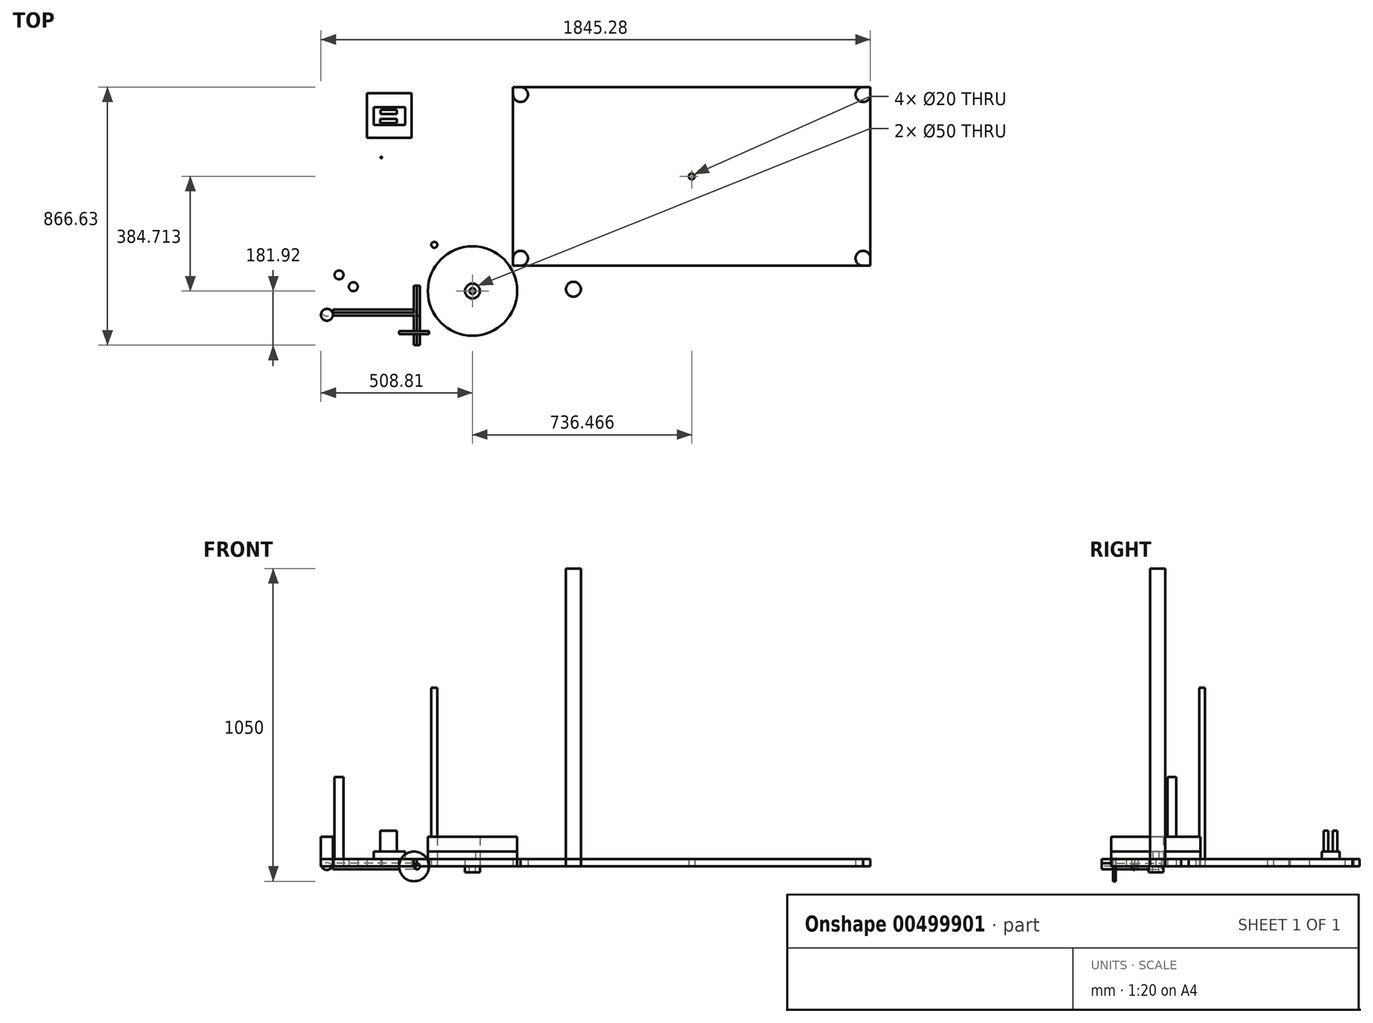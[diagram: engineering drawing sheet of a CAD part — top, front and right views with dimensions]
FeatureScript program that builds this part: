
annotation { "Feature Type Name" : "Feature", "Feature Type Description" : "" }
export const myFeature = defineFeature(function(context is Context, id is Id, definition is map)
    precondition{}
    {
        {
            var Q0;
            Q0=qCreatedBy(makeId("Top.planeOp"),FACE);
            var sketch = newSketch(context, id + "F0", { "sketchPlane" : qUnion([Q0])});
            skCircle(sketch, "E0", {"center": v(0, 0) * mm, "radius": 150 * mm});
            skCircle(sketch, "E1", {"center": v(0, 0) * mm, "radius": 25 * mm});
            skCircle(sketch, "E2", {"center": v(0, 0) * mm, "radius": 10 * mm});
            skCircle(sketch, "E3", {"center": v(-128.12, 155.18) * mm, "radius": 10 * mm});
            skLineSegment(sketch, "E4.bottom", {"start": v(1336.47, 684.71) * mm, "end": v(136.47, 684.71) * mm});
            skLineSegment(sketch, "E4.top", {"start": v(1336.47, 84.71) * mm, "end": v(136.47, 84.71) * mm});
            skLineSegment(sketch, "E4.left", {"start": v(1336.47, 684.71) * mm, "end": v(1336.47, 84.71) * mm});
            skLineSegment(sketch, "E4.right", {"start": v(136.47, 684.71) * mm, "end": v(136.47, 84.71) * mm});
            skCircle(sketch, "E5", {"center": v(161.47, 659.71) * mm, "radius": 25 * mm});
            skCircle(sketch, "E6", {"center": v(161.47, 109.71) * mm, "radius": 25 * mm});
            skCircle(sketch, "E7", {"center": v(1311.47, 659.71) * mm, "radius": 25 * mm});
            skCircle(sketch, "E8", {"center": v(1311.47, 109.71) * mm, "radius": 25 * mm});
            skCircle(sketch, "E9", {"center": v(736.47, 384.71) * mm, "radius": 10 * mm});
            skCircle(sketch, "E10", {"center": v(338.94, 6.05) * mm, "radius": 25 * mm});
            skCircle(sketch, "E11", {"center": v(-448.12, 53.9) * mm, "radius": 15 * mm});
            skCircle(sketch, "E12", {"center": v(-400.17, 14.47) * mm, "radius": 15 * mm});
            skCircle(sketch, "E13", {"center": v(-488.81, -79.96) * mm, "radius": 20 * mm});
            skLineSegment(sketch, "E14", {"start": v(-470.5, -71.92) * mm, "end": v(-191.05, -71.92) * mm});
            skLineSegment(sketch, "E15", {"start": v(-191.3, -81.92) * mm, "end": v(-468.9, -81.92) * mm});
            skLineSegment(sketch, "E16.bottom", {"start": v(-186.3, 18.08) * mm, "end": v(-196.3, 18.08) * mm});
            skLineSegment(sketch, "E16.top", {"start": v(-186.3, -181.92) * mm, "end": v(-196.3, -181.92) * mm});
            skLineSegment(sketch, "E16.left", {"start": v(-186.3, 18.08) * mm, "end": v(-186.3, -181.92) * mm});
            skLineSegment(sketch, "E16.right", {"start": v(-196.3, 18.08) * mm, "end": v(-196.3, -181.92) * mm});
            skPoint(sketch, "E16.middle", {"position": v(-191.3, -81.92) * mm});
            skLineSegment(sketch, "E17.bottom", {"start": v(-146.3, -144.4) * mm, "end": v(-246.3, -144.4) * mm});
            skLineSegment(sketch, "E17.top", {"start": v(-146.3, -134.4) * mm, "end": v(-246.3, -134.4) * mm});
            skLineSegment(sketch, "E17.left", {"start": v(-146.3, -144.4) * mm, "end": v(-146.3, -134.4) * mm});
            skLineSegment(sketch, "E17.right", {"start": v(-246.3, -144.4) * mm, "end": v(-246.3, -134.4) * mm});
            skPoint(sketch, "E17.middle", {"position": v(-196.3, -139.4) * mm});
            skLineSegment(sketch, "E18.right", {"start": v(-236.3, 0) * mm, "end": v(-236.3, 10) * mm});
            skPoint(sketch, "E18.middle", {"position": v(-186.3, 5) * mm});
            skCircle(sketch, "E19", {"center": v(-191.3, -81.92) * mm, "radius": 5 * mm});
            skLineSegment(sketch, "E20", {"start": v(-191.3, -181.92) * mm, "end": v(-191.3, 18.08) * mm});
            skPoint(sketch, "E21", {"position": v(-196.3, -134.4) * mm});
            skPoint(sketch, "E22", {"position": v(-186.3, -134.4) * mm});
            skPoint(sketch, "E23", {"position": v(-196.3, 0) * mm});
            skPoint(sketch, "E24", {"position": v(-186.3, 10) * mm});
            skPoint(sketch, "E25", {"position": v(1086.47, 434.71) * mm});
            skPoint(sketch, "E26", {"position": v(1186.47, 434.71) * mm});
            skPoint(sketch, "E27", {"position": v(1086.47, 334.71) * mm});
            skPoint(sketch, "E28", {"position": v(1186.47, 334.71) * mm});
            skLineSegment(sketch, "E29.bottom", {"start": v(-354.19, 664.69) * mm, "end": v(-204.19, 664.69) * mm});
            skLineSegment(sketch, "E29.top", {"start": v(-354.19, 514.69) * mm, "end": v(-204.19, 514.69) * mm});
            skLineSegment(sketch, "E29.left", {"start": v(-354.19, 664.69) * mm, "end": v(-354.19, 514.69) * mm});
            skLineSegment(sketch, "E29.right", {"start": v(-204.19, 664.69) * mm, "end": v(-204.19, 514.69) * mm});
            skPoint(sketch, "E30", {"position": v(-329.19, 639.69) * mm});
            skPoint(sketch, "E31", {"position": v(-229.19, 639.69) * mm});
            skPoint(sketch, "E32", {"position": v(-329.19, 539.69) * mm});
            skPoint(sketch, "E33", {"position": v(-229.19, 539.69) * mm});
            skLineSegment(sketch, "E34.bottom", {"start": v(-331.08, 616.75) * mm, "end": v(-225.59, 616.75) * mm});
            skLineSegment(sketch, "E34.top", {"start": v(-331.08, 557) * mm, "end": v(-225.59, 557) * mm});
            skLineSegment(sketch, "E34.left", {"start": v(-331.08, 616.75) * mm, "end": v(-331.08, 557) * mm});
            skLineSegment(sketch, "E34.right", {"start": v(-225.59, 616.75) * mm, "end": v(-225.59, 557) * mm});
            skLineSegment(sketch, "E35.bottom", {"start": v(-309.55, 578.54) * mm, "end": v(-254.11, 578.54) * mm});
            skLineSegment(sketch, "E35.top", {"start": v(-309.55, 564) * mm, "end": v(-254.11, 564) * mm});
            skLineSegment(sketch, "E35.left", {"start": v(-309.55, 578.54) * mm, "end": v(-309.55, 564) * mm});
            skLineSegment(sketch, "E35.right", {"start": v(-254.11, 578.54) * mm, "end": v(-254.11, 564) * mm});
            skLineSegment(sketch, "E36.bottom", {"start": v(-309.01, 594.15) * mm, "end": v(-253.58, 594.15) * mm});
            skLineSegment(sketch, "E36.top", {"start": v(-309.01, 608.68) * mm, "end": v(-253.58, 608.68) * mm});
            skLineSegment(sketch, "E36.left", {"start": v(-309.01, 594.15) * mm, "end": v(-309.01, 608.68) * mm});
            skLineSegment(sketch, "E36.right", {"start": v(-253.58, 594.15) * mm, "end": v(-253.58, 608.68) * mm});
            skCircle(sketch, "E37", {"center": v(-306.51, 448.4) * mm, "radius": 2.5 * mm});
            skSolve(sketch);
        }
        {
            var Q0;
            Q0=makeQuery(id+"F0.imprint","IMPRINT",FACE,{"disambiguationData":[TD([[makeQuery(id+"F0.imprint","IMPRINT",EDGE,{"derivedFrom":sQuery(id+"F0.wireOp",EDGE,"E0")}),1.0]])]});
            var Q1;
            Q1=makeQuery(id+"F0.imprint","IMPRINT",FACE,{"disambiguationData":[TD([[makeQuery(id+"F0.imprint","IMPRINT",EDGE,{"derivedFrom":sQuery(id+"F0.wireOp",EDGE,"E1")}),1.0]])]});
            extrude(context, id + "F1", {"entities" : qUnion([Q0, Q1]), "depth" : 50 * mm});
        }
        {
            var Q0;
            Q0=makeQuery(id+"F0.imprint","IMPRINT",FACE,{"disambiguationData":[TD([[makeQuery(id+"F0.imprint","IMPRINT",EDGE,{"derivedFrom":sQuery(id+"F0.wireOp",EDGE,"E1")}),1.0]])]});
            extrude(context, id + "F2", {"entities" : qUnion([Q0]), "oppositeDirection" : true, "depth" : 20 * mm});
        }
        {
            var Q0;
            Q0=makeQuery(id+"F0.imprint","IMPRINT",FACE,{"disambiguationData":[TD([[makeQuery(id+"F0.imprint","IMPRINT",EDGE,{"derivedFrom":sQuery(id+"F0.wireOp",EDGE,"E3")}),1.0]])]});
            var Q1;
            Q1=sQuery(id+"F0.wireOp",EDGE,"E3");
            extrude(context, id + "F3", {"entities" : qUnion([Q0]), "surfaceEntities" : qUnion([Q1]), "depth" : 600 * mm});
        }
        {
            var Q0;
            Q0=makeQuery(id+"F0.imprint","IMPRINT",FACE,{"disambiguationData":[TD([[makeQuery(id+"F0.imprint","IMPRINT",EDGE,{"derivedFrom":sQuery(id+"F0.wireOp",EDGE,"E9")}),-1.0]])]});
            extrude(context, id + "F4", {"entities" : qUnion([Q0]), "depth" : 25 * mm});
        }
        {
            var Q0;
            Q0=makeQuery(id+"F0.imprint","IMPRINT",FACE,{"disambiguationData":[TD([[makeQuery(id+"F0.imprint","IMPRINT",EDGE,{"derivedFrom":sQuery(id+"F0.wireOp",EDGE,"E10")}),1.0]])]});
            extrude(context, id + "F5", {"entities" : qUnion([Q0]), "depth" : 1000 * mm});
        }
        {
            var Q0;
            Q0=makeQuery(id+"F0.imprint","IMPRINT",FACE,{"disambiguationData":[TD([[makeQuery(id+"F0.imprint","IMPRINT",EDGE,{"derivedFrom":sQuery(id+"F0.wireOp",EDGE,"E11")}),1.0]])]});
            var Q1;
            Q1=sQuery(id+"F0.wireOp",EDGE,"E11");
            extrude(context, id + "F6", {"entities" : qUnion([Q0]), "surfaceEntities" : qUnion([Q1]), "depth" : 300 * mm});
        }
        {
            var Q0;
            {var subQ0=sQuery(id+"F0.wireOp",EDGE,"E13");var subQ1=makeQuery(id+"F0.imprint","INTERSECT",VERTEX,{"derivedFrom":[subQ0,sQuery(id+"F0.wireOp",EDGE,"E14")]});Q0=makeQuery(id+"F0.imprint","IMPRINT",FACE,{"disambiguationData":[TD([[makeQuery(id+"F0.imprint","IMPRINT",EDGE,{"disambiguationData":[TD([[subQ1,-1.0]])],"derivedFrom":subQ0}),1.0]])]});}
            var Q1;
            Q1=makeQuery(id+"F0.imprint","IMPRINT",FACE,{"disambiguationData":[TD([[makeQuery(id+"F0.imprint","IMPRINT",EDGE,{"derivedFrom":sQuery(id+"F0.wireOp",EDGE,"E1")}),-1.0]])]});
            var Q2;
            Q2 = qConstructionFilter(qBodyType(qCreatedBy(id + "F0" ,EDGE), BodyType.WIRE), ConstructionObject.NO);
            extrude(context, id + "F7", {"entities" : qUnion([Q0, Q1]), "surfaceEntities" : qUnion([Q2]), "depth" : 100 * mm});
        }
        {
            var Q0;
            {var subQ1=sQuery(id+"F0.wireOp",EDGE,"E14");Q0=makeQuery(id+"F0.imprint","IMPRINT",FACE,{"disambiguationData":[TD([[makeQuery(id+"F0.imprint","IMPRINT",EDGE,{"derivedFrom":subQ1}),-1.0]])]});}
            var Q1;
            Q1=sQuery(id+"F0.wireOp",EDGE,"E14");
            revolve(context, id + "F8", {"entities" : qUnion([Q0]), "axis" : qUnion([Q1]), "revolveType" : RevolveType.FULL});
        }
        {
            var Q0;
            {var subQ0=sQuery(id+"F0.wireOp",EDGE,"E18.bottom");var subQ1=sQuery(id+"F0.wireOp",EDGE,"E16.left");var subQ2=makeQuery(id+"F0.imprint","INTERSECT",VERTEX,{"derivedFrom":[subQ1,subQ0]});Q0=makeQuery(id+"F0.imprint","IMPRINT",FACE,{"disambiguationData":[TD([[makeQuery(id+"F0.imprint","IMPRINT",EDGE,{"disambiguationData":[TD([[subQ2,-1.0]])],"derivedFrom":subQ1}),-1.0]])]});}
            var Q1;
            {var subQ0=sQuery(id+"F0.wireOp",EDGE,"E16.left");var subQ1=sQuery(id+"F0.wireOp",EDGE,"E16.bottom");var subQ2=makeQuery(id+"F0.imprint","INTERSECT",VERTEX,{"derivedFrom":[subQ1,subQ0]});Q1=makeQuery(id+"F0.imprint","IMPRINT",FACE,{"disambiguationData":[TD([[makeQuery(id+"F0.imprint","IMPRINT",EDGE,{"disambiguationData":[TD([[subQ2,-1.0]])],"derivedFrom":subQ1}),1.0]])]});}
            var Q2;
            {var subQ0=sQuery(id+"F0.wireOp",EDGE,"E16.right");var subQ1=sQuery(id+"F0.wireOp",EDGE,"E16.bottom");var subQ2=makeQuery(id+"F0.imprint","INTERSECT",VERTEX,{"derivedFrom":[subQ1,subQ0]});Q2=makeQuery(id+"F0.imprint","IMPRINT",FACE,{"disambiguationData":[TD([[makeQuery(id+"F0.imprint","IMPRINT",EDGE,{"disambiguationData":[TD([[subQ2,1.0]])],"derivedFrom":subQ1}),1.0]])]});}
            var Q3;
            {var subQ0=sQuery(id+"F0.wireOp",EDGE,"E18.top");var subQ1=sQuery(id+"F0.wireOp",EDGE,"E16.right");var subQ2=makeQuery(id+"F0.imprint","INTERSECT",VERTEX,{"derivedFrom":[subQ1,subQ0]});Q3=makeQuery(id+"F0.imprint","IMPRINT",FACE,{"disambiguationData":[TD([[makeQuery(id+"F0.imprint","IMPRINT",EDGE,{"disambiguationData":[TD([[subQ2,-1.0]])],"derivedFrom":subQ1}),1.0]])]});}
            var Q4;
            {var subQ0=sQuery(id+"F0.wireOp",EDGE,"E18.top");var subQ1=sQuery(id+"F0.wireOp",EDGE,"E16.left");var subQ2=makeQuery(id+"F0.imprint","INTERSECT",VERTEX,{"derivedFrom":[subQ1,subQ0]});Q4=makeQuery(id+"F0.imprint","IMPRINT",FACE,{"disambiguationData":[TD([[makeQuery(id+"F0.imprint","IMPRINT",EDGE,{"disambiguationData":[TD([[subQ2,-1.0]])],"derivedFrom":subQ1}),-1.0]])]});}
            var Q5;
            {var subQ0=sQuery(id+"F0.wireOp",EDGE,"E18.bottom");var subQ1=sQuery(id+"F0.wireOp",EDGE,"E16.right");var subQ2=makeQuery(id+"F0.imprint","INTERSECT",VERTEX,{"derivedFrom":[subQ1,subQ0]});Q5=makeQuery(id+"F0.imprint","IMPRINT",FACE,{"disambiguationData":[TD([[makeQuery(id+"F0.imprint","IMPRINT",EDGE,{"disambiguationData":[TD([[subQ2,-1.0]])],"derivedFrom":subQ1}),1.0]])]});}
            var Q6;
            {var subQ0=sQuery(id+"F0.wireOp",EDGE,"E19");var subQ1=sQuery(id+"F0.wireOp",EDGE,"E16.right");var subQ2=makeQuery(id+"F0.imprint","INTERSECT",VERTEX,{"derivedFrom":[subQ1,subQ0]});Q6=makeQuery(id+"F0.imprint","IMPRINT",FACE,{"disambiguationData":[TD([[makeQuery(id+"F0.imprint","IMPRINT",EDGE,{"disambiguationData":[TD([[subQ2,-1.0]])],"derivedFrom":subQ1}),1.0]])]});}
            var Q7;
            {var subQ0=sQuery(id+"F0.wireOp",EDGE,"E19");var subQ1=sQuery(id+"F0.wireOp",EDGE,"E16.left");var subQ2=makeQuery(id+"F0.imprint","INTERSECT",VERTEX,{"derivedFrom":[subQ1,subQ0]});Q7=makeQuery(id+"F0.imprint","IMPRINT",FACE,{"disambiguationData":[TD([[makeQuery(id+"F0.imprint","IMPRINT",EDGE,{"disambiguationData":[TD([[subQ2,-1.0]])],"derivedFrom":subQ1}),-1.0]])]});}
            var Q8;
            {var subQ0=sQuery(id+"F0.wireOp",EDGE,"E16.left");var subQ1=sQuery(id+"F0.wireOp",EDGE,"E16.top");var subQ2=makeQuery(id+"F0.imprint","INTERSECT",VERTEX,{"derivedFrom":[subQ1,subQ0]});Q8=makeQuery(id+"F0.imprint","IMPRINT",FACE,{"disambiguationData":[TD([[makeQuery(id+"F0.imprint","IMPRINT",EDGE,{"disambiguationData":[TD([[subQ2,-1.0]])],"derivedFrom":subQ1}),-1.0]])]});}
            var Q9;
            {var subQ0=sQuery(id+"F0.wireOp",EDGE,"E16.right");var subQ1=sQuery(id+"F0.wireOp",EDGE,"E16.top");var subQ2=makeQuery(id+"F0.imprint","INTERSECT",VERTEX,{"derivedFrom":[subQ1,subQ0]});Q9=makeQuery(id+"F0.imprint","IMPRINT",FACE,{"disambiguationData":[TD([[makeQuery(id+"F0.imprint","IMPRINT",EDGE,{"disambiguationData":[TD([[subQ2,1.0]])],"derivedFrom":subQ1}),-1.0]])]});}
            var Q10;
            {var subQ0=sQuery(id+"F0.wireOp",EDGE,"E17.top");var subQ1=sQuery(id+"F0.wireOp",EDGE,"E16.left");var subQ2=makeQuery(id+"F0.imprint","INTERSECT",VERTEX,{"derivedFrom":[subQ1,subQ0]});Q10=makeQuery(id+"F0.imprint","IMPRINT",FACE,{"disambiguationData":[TD([[makeQuery(id+"F0.imprint","IMPRINT",EDGE,{"disambiguationData":[TD([[subQ2,-1.0]])],"derivedFrom":subQ1}),-1.0]])]});}
            var Q11;
            {var subQ0=sQuery(id+"F0.wireOp",EDGE,"E17.top");var subQ1=sQuery(id+"F0.wireOp",EDGE,"E16.right");var subQ2=makeQuery(id+"F0.imprint","INTERSECT",VERTEX,{"derivedFrom":[subQ1,subQ0]});Q11=makeQuery(id+"F0.imprint","IMPRINT",FACE,{"disambiguationData":[TD([[makeQuery(id+"F0.imprint","IMPRINT",EDGE,{"disambiguationData":[TD([[subQ2,-1.0]])],"derivedFrom":subQ1}),1.0]])]});}
            var Q12;
            Q12=sQuery(id+"F0.wireOp",EDGE,"E16.left");
            revolve(context, id + "F9", {"entities" : qUnion([Q0, Q1, Q2, Q3, Q4, Q5, Q6, Q7, Q8, Q9, Q10, Q11]), "axis" : qUnion([Q12]), "revolveType" : RevolveType.FULL});
        }
        {
            var Q0;
            Q0=sQuery(id+"F0.wireOp",EDGE,"E19");
            extrude(context, id + "F10", {"bodyType" : ToolBodyType.SURFACE, "surfaceEntities" : qUnion([Q0]), "oppositeDirection" : true, "depth" : 25 * mm});
        }
        {
            var Q0;
            Q0=sQuery(id+"F0.wireOp",EDGE,"E0");
            extrude(context, id + "F11", {"bodyType" : ToolBodyType.SURFACE, "surfaceEntities" : qUnion([Q0]), "depth" : 25 * mm});
        }
        {
            var Q0;
            {var subQ5=sQuery(id+"F0.wireOp",EDGE,"E17.left");Q0=makeQuery(id+"F0.imprint","IMPRINT",FACE,{"disambiguationData":[TD([[makeQuery(id+"F0.imprint","IMPRINT",EDGE,{"derivedFrom":subQ5}),1.0]])]});}
            var Q1;
            {var subQ5=sQuery(id+"F0.wireOp",EDGE,"E17.right");Q1=makeQuery(id+"F0.imprint","IMPRINT",FACE,{"disambiguationData":[TD([[makeQuery(id+"F0.imprint","IMPRINT",EDGE,{"derivedFrom":subQ5}),-1.0]])]});}
            var Q2;
            Q2=sQuery(id+"F0.wireOp",EDGE,"E16.right");
            revolve(context, id + "F12", {"operationType" : NewBodyOperationType.ADD, "entities" : qUnion([Q0, Q1]), "axis" : qUnion([Q2]), "revolveType" : RevolveType.FULL});
        }
        {
            var Q0;
            Q0 = qSketchRegion(id + "F0", true);
            extrude(context, id + "F13", {"entities" : qUnion([Q0]), "depth" : 25 * mm});
        }
        {
            var Q0;
            Q0=makeQuery(id+"F0.imprint","IMPRINT",FACE,{"disambiguationData":[TD([[makeQuery(id+"F0.imprint","IMPRINT",EDGE,{"derivedFrom":sQuery(id+"F0.wireOp",EDGE,"E34.bottom")}),-1.0]])]});
            extrude(context, id + "F14", {"entities" : qUnion([Q0]), "operationType" : NewBodyOperationType.ADD, "depth" : 50 * mm});
        }
        {
            var Q0;
            Q0=makeQuery(id+"F0.imprint","IMPRINT",FACE,{"disambiguationData":[TD([[makeQuery(id+"F0.imprint","IMPRINT",EDGE,{"derivedFrom":sQuery(id+"F0.wireOp",EDGE,"E36.bottom")}),1.0]])]});
            var Q1;
            Q1=makeQuery(id+"F0.imprint","IMPRINT",FACE,{"disambiguationData":[TD([[makeQuery(id+"F0.imprint","IMPRINT",EDGE,{"derivedFrom":sQuery(id+"F0.wireOp",EDGE,"E35.bottom")}),-1.0]])]});
            extrude(context, id + "F15", {"entities" : qUnion([Q0, Q1]), "operationType" : NewBodyOperationType.ADD, "depth" : 120 * mm});
        }
    });
